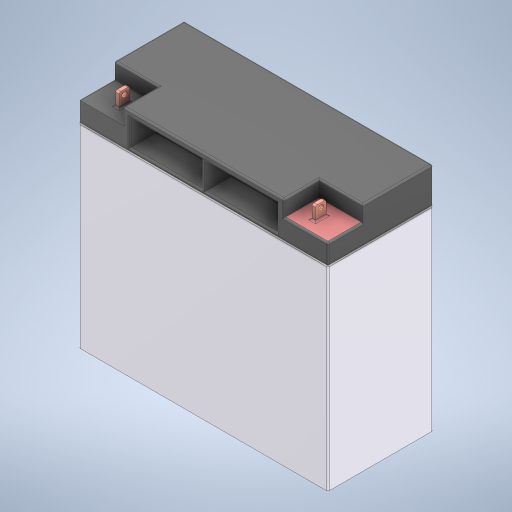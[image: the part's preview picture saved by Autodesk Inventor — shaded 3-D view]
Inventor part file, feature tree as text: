
AUTODESK INVENTOR PART (.ipt)
format: ipt  version: 2024 (Build 280153000, 153)  size: 308,224 bytes
history: native  units: in
note: dims shown in document units (in); Inventor stores cm internally (conversion verified against a paired STEP export)
features: fillet x1
ambient origin geometry x8: Origin, YZ Plane, XZ Plane, XY Plane, X Axis, Y Axis, Z Axis, Center Point
bodies: Solid1 (feature_tree)
feature tree (1):
  fillet  "Fillet4"  [1 undecoded]
note: 1 required parameter value undecoded (feature->parameter linkage not recoverable at this tier; creation-order binding heuristic only, values carry confidence <= 0.55)
